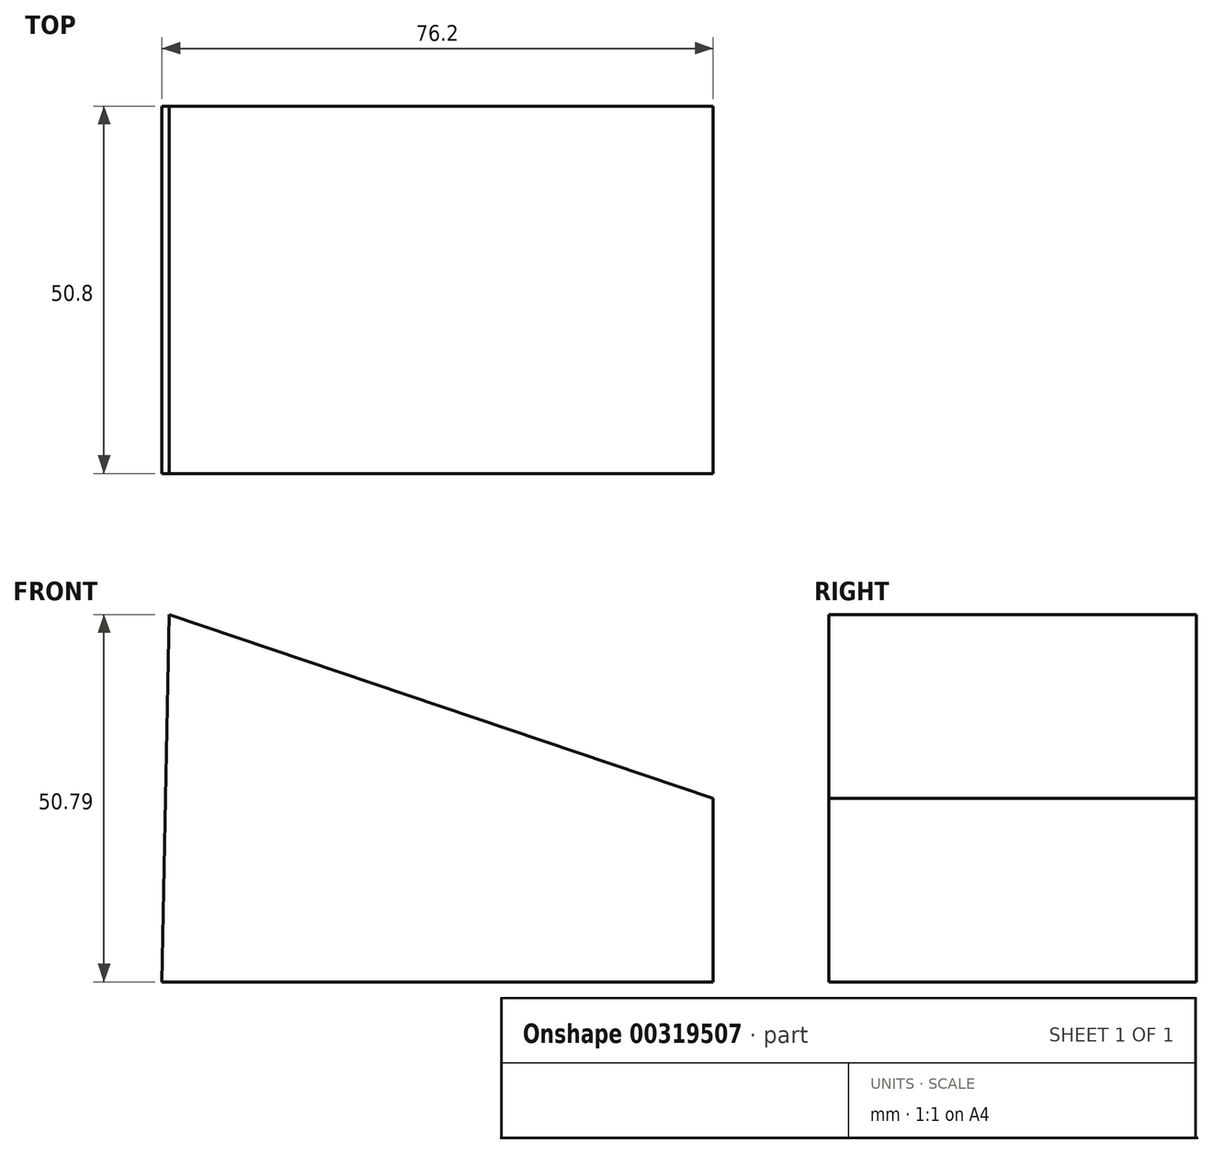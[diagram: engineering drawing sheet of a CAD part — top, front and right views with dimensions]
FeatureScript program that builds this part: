
annotation { "Feature Type Name" : "Feature", "Feature Type Description" : "" }
export const myFeature = defineFeature(function(context is Context, id is Id, definition is map)
    precondition{}
    {
        {
            var Q0;
            Q0=qCreatedBy(makeId("Front.planeOp"),FACE);
            var sketch = newSketch(context, id + "F0", { "sketchPlane" : qUnion([Q0])});
            skLineSegment(sketch, "E0", {"start": v(-57.44, -37.6) * mm, "end": v(18.76, -37.6) * mm});
            skLineSegment(sketch, "E1", {"start": v(18.76, -37.6) * mm, "end": v(18.76, -12.2) * mm});
            skLineSegment(sketch, "E2", {"start": v(18.76, -12.2) * mm, "end": v(-56.47, 13.18) * mm});
            skLineSegment(sketch, "E3", {"start": v(-56.47, 13.18) * mm, "end": v(-57.44, -37.6) * mm});
            skSolve(sketch);
        }
        {
            var Q0;
            Q0=makeQuery(id+"F0.imprint","IMPRINT",FACE,{"disambiguationData":[TD([[makeQuery(id+"F0.imprint","IMPRINT",EDGE,{"derivedFrom":sQuery(id+"F0.wireOp",EDGE,"E0")}),1.0]])]});
            extrude(context, id + "F1", {"entities" : qUnion([Q0]), "depth" : 50.8 * mm});
        }
    });
